# Revit family: 3032852 Sylvania_Giotto 335 LED_Surface Mounted
name_source: partatom
category: Lighting Fixtures
revit_build: Autodesk Revit 2017 (Build: 20190507_1515(x64)
units: mm (PartAtom-declared; Revit-internal decimal feet)

## family parameters
Cut with Voids When Loaded = No
Host = Face
Light Source = Yes
OmniClass Number = 23.80.70.11.17
OmniClass Title = Specialized Lighting by Location or Use
Part Type = Normal
Room Calculation Point = No
Round Connector Dimension = Use Diameter
Shared = No

## types (1)
- Giotto335 sur ww DB
    Apparent Load = 19 VA
    Assembly Code = D5020200
    Body Material = Polycarbonate_Sylvania_Giotto_White
    Catalog Number = 3032852 Giotto335 sur ww DB
    Color Filter = 16777215
    Default Elevation = 0 mm  [stored 0 ft]
    Description = Surface or recessed mount versions available. Ideal for general lighting in public areas. Microwave presence detection versions. 3 hour emergency light versions with integrated gear. Up to 1200lm neutral white
    Diameter = 335 mm  [stored 1.09908 ft]
    Diffuser Material = Polycarbonate_Sylvania_Giotto_Opal
    Dimming Lamp Color Temperature Shift = <None>
    Drive Current = 700 mA
    Electrical Protection = CLASS II
    Emit Shape Visible in Rendering = No
    Emit from Circle Diameter = 319 mm
    Height = 110 mm  [stored 0.360892 ft]
    IK Rating = IK10
    IP Rating = IP44
    Lamp = 19W
    Lamp Comments = Integrated LED
    Life = 50 000 h
    Manufacturer = Feilo Sylvania
    Model = Giotto335 sur ww DB
    Photometric Web File = 3032852_GiottoLED33525WSurfaceMountedWarmWhiteDB-121664.ies
    Product Family = GIOTTO 335 LED - SURFACE MOUNTED
    Product Page URL = http://www.sylvania-lighting.com
    Tilt Angle = -90°
    URL = http://www.sylvania-lighting.com
    Voltage = 230 V
    Voltage Comments = UNV (Universal Voltage; 220-240 Volt)
    Weight = 1 kg

note: [stored X ft] marks values corroborated as IEEE doubles in the binary element streams (Revit-internal decimal feet)

## geometry (parser evidence)
native form markers: Sweep x3
no freeform markers — native parametric forms only
